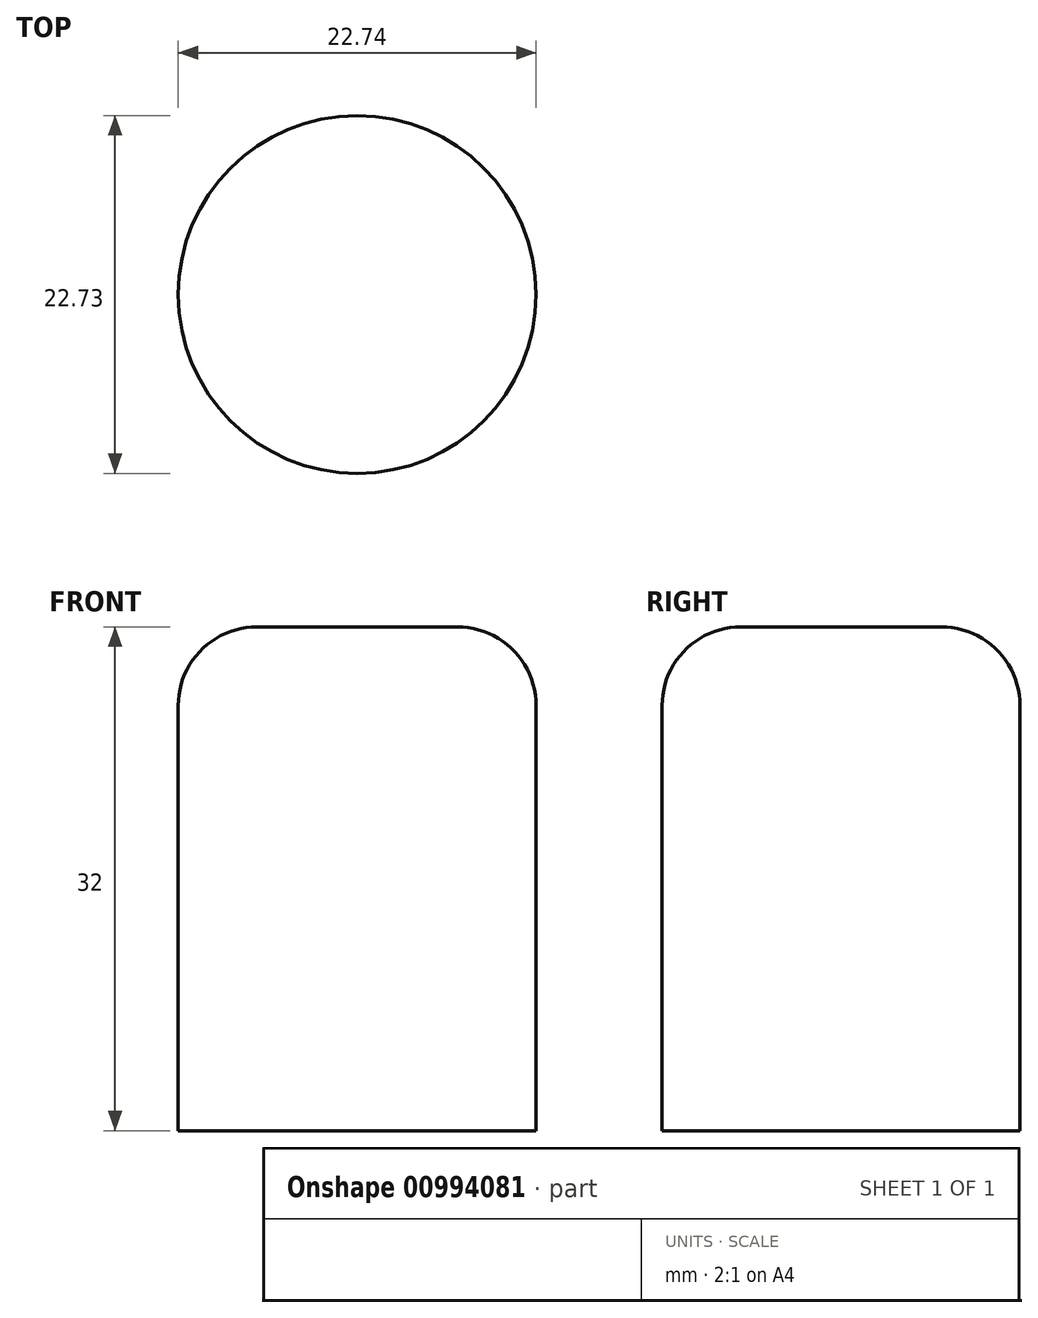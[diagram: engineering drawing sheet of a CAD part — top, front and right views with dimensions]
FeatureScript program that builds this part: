
annotation { "Feature Type Name" : "Feature", "Feature Type Description" : "" }
export const myFeature = defineFeature(function(context is Context, id is Id, definition is map)
    precondition{}
    {
        {
            var Q0;
            Q0=qCreatedBy(makeId("Top.planeOp"),FACE);
            var sketch = newSketch(context, id + "F0", { "sketchPlane" : qUnion([Q0])});
            skLineSegment(sketch, "E0.bottom", {"start": v(-21.87, 0) * mm, "end": v(21.47, 0) * mm});
            skLineSegment(sketch, "E0.top", {"start": v(-21.87, 43.14) * mm, "end": v(21.47, 43.14) * mm});
            skLineSegment(sketch, "E0.left", {"start": v(-21.87, 0) * mm, "end": v(-21.87, 43.14) * mm});
            skLineSegment(sketch, "E0.right", {"start": v(21.47, 0) * mm, "end": v(21.47, 43.14) * mm});
            skLineSegment(sketch, "E1.bottom", {"start": v(-32.7, 14.25) * mm, "end": v(-82.46, 14.25) * mm});
            skLineSegment(sketch, "E1.top", {"start": v(-32.7, -24.68) * mm, "end": v(-82.46, -24.68) * mm});
            skLineSegment(sketch, "E1.left", {"start": v(-32.7, 14.25) * mm, "end": v(-32.7, -24.68) * mm});
            skLineSegment(sketch, "E1.right", {"start": v(-82.46, 14.25) * mm, "end": v(-82.46, -24.68) * mm});
            skCircle(sketch, "E2", {"center": v(0, 23.47) * mm, "radius": 11.37 * mm});
            skCircle(sketch, "E3", {"center": v(-60.4, -5.22) * mm, "radius": 9.68 * mm});
            skPoint(sketch, "E3.centerSnap0", {"position": v(-32.7, -5.22) * mm});
            skSolve(sketch);
        }
        {
            var Q0;
            Q0=makeQuery(id+"F0.imprint","IMPRINT",FACE,{"disambiguationData":[TD([[makeQuery(id+"F0.imprint","IMPRINT",EDGE,{"derivedFrom":sQuery(id+"F0.wireOp",EDGE,"E2")}),1.0]])]});
            extrude(context, id + "F1", {"entities" : qUnion([Q0]), "depth" : 25 * mm, "offsetDistance" : 25 * mm});
        }
        {
            var Q0;
            Q0=makeQuery(id+"F1.opExtrude","CAP_FACE",FACE,{"disambiguationData":[OSD([sQuery(id+"F0.wireOp",EDGE,"E2")])],"isStart":false});
            extrude(context, id + "F2", {"entities" : qUnion([Q0]), "operationType" : NewBodyOperationType.ADD, "oppositeDirection" : true, "depth" : 32 * mm, "offsetDistance" : 25 * mm});
        }
        {
            var Q0;
            Q0=makeQuery(id+"F1.opExtrude","CAP_EDGE",EDGE,{"disambiguationData":[OSD([sQuery(id+"F0.wireOp",EDGE,"E2")])],"isStart":false});
            fillet(context, id + "F3", {"entities" : qUnion([Q0]), "radius" : 5 * mm, "tangentPropagation" : true, "allowEdgeOverflow" : false});
        }
    });
